# Revit family: ITK_Комплект для защиты сварки_40мм
name_source: partatom
category: Обобщенные модели
units: mm (PartAtom-declared; Revit-internal decimal feet)

## family parameters
Всегда вертикально = Да
Может служить основой для арматурных стержней = Нет
На основе рабочей плоскости = Нет
Общий = Нет
При загрузке вырезать с полостями = Нет
Размер круглого соединителя = Использовать диаметр
Тип детали = Нормальный
Точка расчета площади = Нет

## types (2) — shared parameters
ADSK_URL страницы изделия = https://www.itk-group.ru
ADSK_Версия Revit = 2019
ADSK_Версия семейства = 1.0
ADSK_Группирование = I. ЩИТЫ И ПУЛЬТЫ
ADSK_Единица измерения = шт
ADSK_Завод-изготовитель = IEK
ADSK_Материал наименование = Сталь
IEK_URL = https://www.itk-group.ru
IEK_Описание = Изготовлены из высококачественных материалов.
Соответствие международным стандартам и ГОСТ Р.
URL = https://www.iek.ru
Изготовитель = ITK
Материал = Окраска - RAL 7035
zero-valued in all types: ADSK_Масса

## per-type parameters (varying)
| type | ADSK_Код изделия | ADSK_Наименование | IEK_Цена за единицу |
| 40 мм | FOKDZS-40 | ITK Комплект для защиты сварки, 40мм | 12.66 |
| 60 мм | FOKDZS-60 | ITK Комплект для защиты сварки, 60мм | 13.62 |

note: column(s) folded — value = type name in every type: Высота
